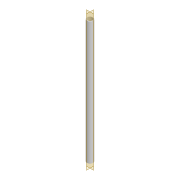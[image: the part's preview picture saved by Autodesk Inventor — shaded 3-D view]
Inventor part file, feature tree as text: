
AUTODESK INVENTOR PART (.ipt)
format: ipt  version: 2022 (Build 260153000, 153)  size: 77,824 bytes
history: native  units: mm
features: extrude x1, sketch x1
ambient origin geometry x8: Origin, YZ Plane, XZ Plane, XY Plane, X Axis, Y Axis, Z Axis, Center Point
bodies: Body1 (feature_tree)
feature tree (2):
  extrude  "Extrusion2"  Depth=238.0mm
  sketch  "Sketch2"  dims[d6=10.0mm d7=12.0mm d8=238.0mm d9=0.0mm]
